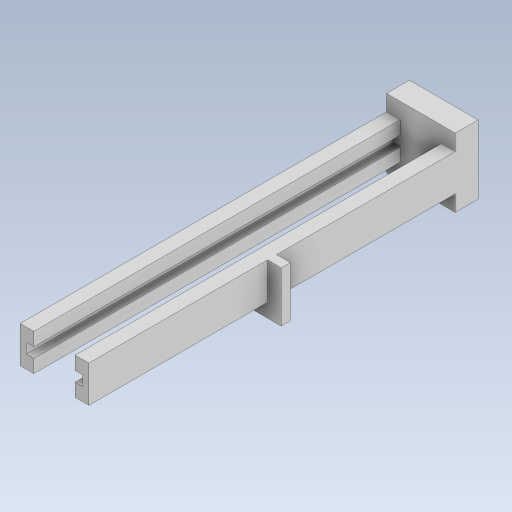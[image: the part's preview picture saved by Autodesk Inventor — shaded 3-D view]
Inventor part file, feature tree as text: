
AUTODESK INVENTOR PART (.ipt)
format: ipt  version: 2023.5 (Build 275446000, 446)  size: 339,456 bytes
history: native  units: in
note: dims shown in document units (in); Inventor stores cm internally (conversion verified against a paired STEP export)
features: extrude x4, sketch x3
ambient origin geometry x8: Origin, YZ Plane, XZ Plane, XY Plane, X Axis, Y Axis, Z Axis, Center Point
bodies: Solid1 (feature_tree)
feature tree (7):
  sketch  "Sketch1"  dims[d0=0.5906in d1=0.5906in]
  extrude  "Extrusion1"  Depth=0.5906in
  extrude  "Extrusion2"  Depth=0.315in
  extrude  "Extrusion3"  Depth=0.1181in
  extrude  "Extrusion4"  Depth=0.0866in
  sketch  "Sketch2"  dims[d2=0.1181in d3=0.315in]
  sketch  "Sketch3"  dims[d5=0.1772in d6=0.126in d7=0.0866in d8=0.1969in d9=0.0in d10=3.1496in d11=0.0in d12=0.0787in d13=0.1181in d14=0.0in d15=0.0787in d16=0.1181in d17=0.0in]
